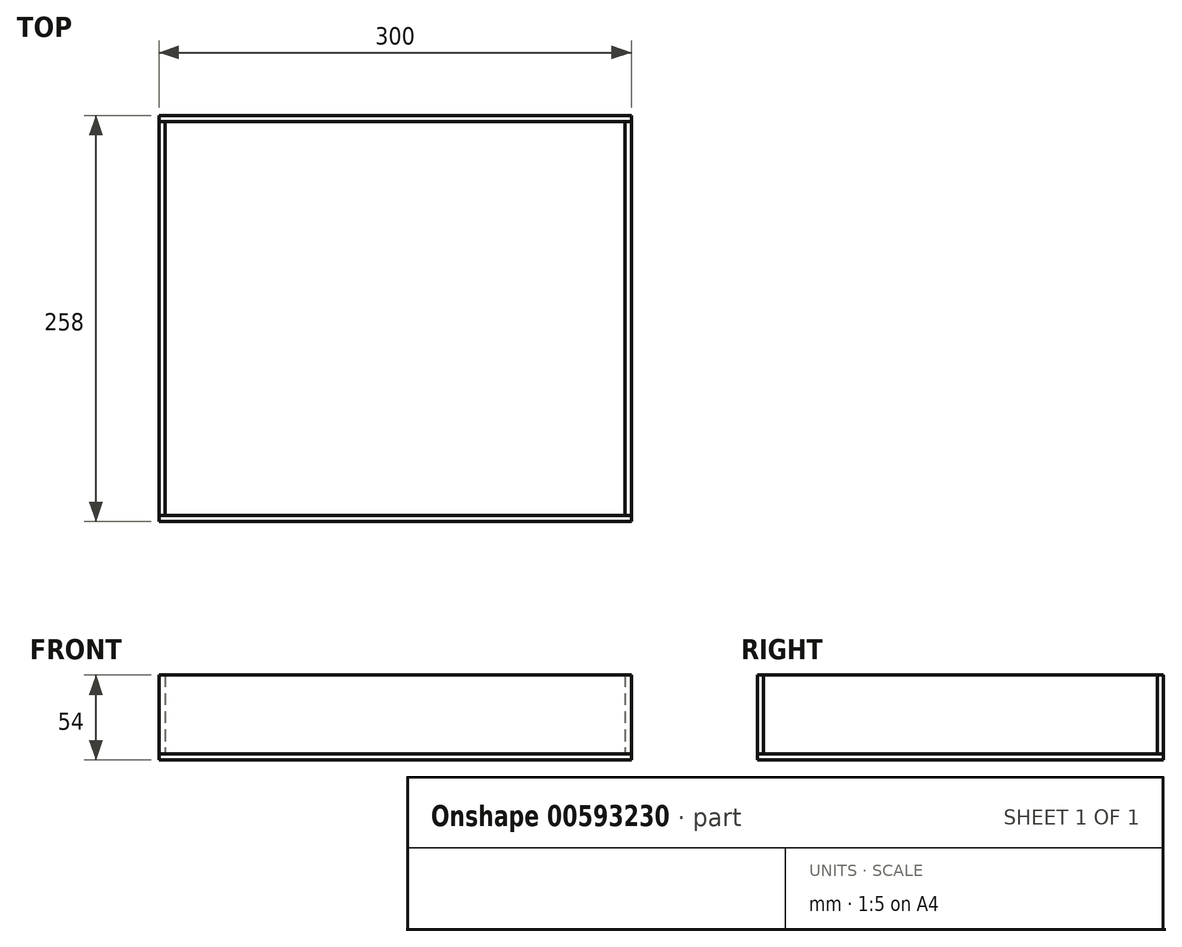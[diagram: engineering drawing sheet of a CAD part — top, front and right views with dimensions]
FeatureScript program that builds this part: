
annotation { "Feature Type Name" : "Feature", "Feature Type Description" : "" }
export const myFeature = defineFeature(function(context is Context, id is Id, definition is map)
    precondition{}
    {
        {
            var Q0;
            Q0=qCreatedBy(makeId("Top.planeOp"),FACE);
            var sketch = newSketch(context, id + "F0", { "sketchPlane" : qUnion([Q0])});
            skLineSegment(sketch, "E0.bottom", {"start": v(0, 258) * mm, "end": v(300, 258) * mm});
            skLineSegment(sketch, "E0.top", {"start": v(0, 0) * mm, "end": v(300, 0) * mm});
            skLineSegment(sketch, "E0.left", {"start": v(0, 258) * mm, "end": v(0, 0) * mm});
            skLineSegment(sketch, "E0.right", {"start": v(300, 258) * mm, "end": v(300, 0) * mm});
            skLineSegment(sketch, "E1", {"start": v(0, 254) * mm, "end": v(300, 254) * mm});
            skLineSegment(sketch, "E2", {"start": v(296, 254) * mm, "end": v(296, 4) * mm});
            skLineSegment(sketch, "E3", {"start": v(300, 4) * mm, "end": v(0, 4) * mm});
            skLineSegment(sketch, "E4", {"start": v(4, 254) * mm, "end": v(4, 4) * mm});
            skSolve(sketch);
        }
        {
            var Q0;
            Q0 = qSketchRegion(id + "F0", true);
            var Q1;
            {var subQ0=sQuery(id+"F0.wireOp",EDGE,"E2");Q1=makeQuery(id+"F0.imprint","IMPRINT",FACE,{"disambiguationData":[TD([[makeQuery(id+"F0.imprint","IMPRINT",EDGE,{"derivedFrom":subQ0}),-1.0]])]});}
            extrude(context, id + "F1", {"entities" : qUnion([Q0, Q1]), "oppositeDirection" : true, "depth" : 4 * mm, "offsetDistance" : 25 * mm});
        }
        {
            var Q0;
            {var subQ4=sQuery(id+"F0.wireOp",EDGE,"E0.top");Q0=makeQuery(id+"F0.imprint","IMPRINT",FACE,{"disambiguationData":[TD([[makeQuery(id+"F0.imprint","IMPRINT",EDGE,{"derivedFrom":subQ4}),1.0]])]});}
            extrude(context, id + "F2", {"entities" : qUnion([Q0]), "depth" : 50 * mm, "offsetDistance" : 25 * mm});
        }
        {
            var Q0;
            {var subQ5=sQuery(id+"F0.wireOp",EDGE,"E4");Q0=makeQuery(id+"F0.imprint","IMPRINT",FACE,{"disambiguationData":[TD([[makeQuery(id+"F0.imprint","IMPRINT",EDGE,{"derivedFrom":subQ5}),-1.0]])]});}
            extrude(context, id + "F3", {"entities" : qUnion([Q0]), "depth" : 50 * mm, "offsetDistance" : 25 * mm});
        }
        {
            var Q0;
            {var subQ4=sQuery(id+"F0.wireOp",EDGE,"E0.bottom");Q0=makeQuery(id+"F0.imprint","IMPRINT",FACE,{"disambiguationData":[TD([[makeQuery(id+"F0.imprint","IMPRINT",EDGE,{"derivedFrom":subQ4}),-1.0]])]});}
            extrude(context, id + "F4", {"entities" : qUnion([Q0]), "depth" : 50 * mm, "offsetDistance" : 25 * mm});
        }
        {
            var Q0;
            {var subQ5=sQuery(id+"F0.wireOp",EDGE,"E2");Q0=makeQuery(id+"F0.imprint","IMPRINT",FACE,{"disambiguationData":[TD([[makeQuery(id+"F0.imprint","IMPRINT",EDGE,{"derivedFrom":subQ5}),1.0]])]});}
            extrude(context, id + "F5", {"entities" : qUnion([Q0]), "depth" : 50 * mm, "offsetDistance" : 25 * mm});
        }
    });
